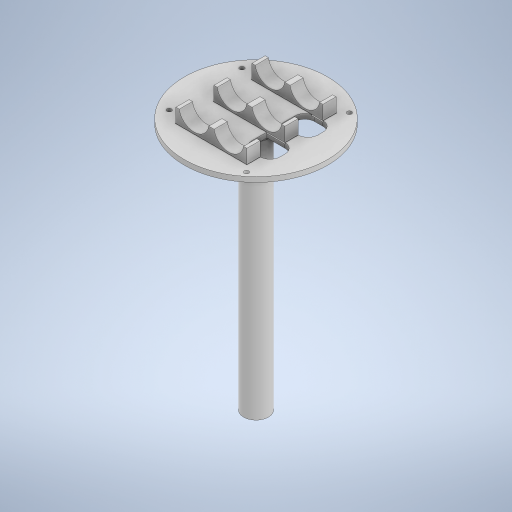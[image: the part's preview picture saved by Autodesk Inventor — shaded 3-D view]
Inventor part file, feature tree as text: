
AUTODESK INVENTOR PART (.ipt)
format: ipt  version: 2024 (Build 280153000, 153)  size: 502,272 bytes
history: native  units: mm
features: extrude x12, sketch x9, projected_geometry x5, fillet x3, other x2, chamfer x1
ambient origin geometry x8: Origin, YZ Plane, XZ Plane, XY Plane, X Axis, Y Axis, Z Axis, Center Point
bodies: Solide1 (feature_tree), Solide2 (feature_tree), Solide3 (feature_tree)
feature tree (32):
  sketch  "Esquisse1"
  extrude  "Extrusion1"  Depth=10.0mm TaperAngle=0.0deg
  extrude  "Extrusion2"  Depth=3.0mm TaperAngle=0.0deg
  sketch  "Esquisse2"
  extrude  "Extrusion3"  Depth=10.95mm
  extrude  "Extrusion4"  TaperAngle=0.0deg  [1 undecoded]
  sketch  "Esquisse3"
  extrude  "Extrusion5"  Depth=43.0mm
  extrude  "Extrusion6"  Depth=1.5mm
  chamfer  "Chanfrein1"  [1 undecoded]
  extrude  "Extrusion7"  Depth=86.7mm
  other  "Plan de construction1"
  sketch  "Esquisse6"
  extrude  "Extrusion8"  Depth=15.0mm
  extrude  "Extrusion9"  Depth=17.0mm
  fillet  "Congé1"  Radius=17.0mm
  fillet  "Congé2"  Radius=10.0mm
  fillet  "Congé3"  Radius=150.0mm
  other  "Scission1"
  extrude  "Extrusion10"  Depth=4.0mm TaperAngle=45.0deg
  extrude  "Extrusion11"  Depth=8.0mm
  extrude  "Extrusion12"  Depth=150.0mm TaperAngle=0.0deg
  projected_geometry  "Boucle projetée1"
  sketch  "Esquisse4"
  sketch  "Esquisse5"
  sketch  "Esquisse8"
  projected_geometry  "Boucle projetée3"
  sketch  "Esquisse9"
  projected_geometry  "Boucle projetée4"
  projected_geometry  "Boucle projetée5"
  projected_geometry  "Boucle projetée6"
  sketch  "Esquisse10"
note: 2 required parameter values undecoded (feature->parameter linkage not recoverable at this tier; creation-order binding heuristic only, values carry confidence <= 0.55)
